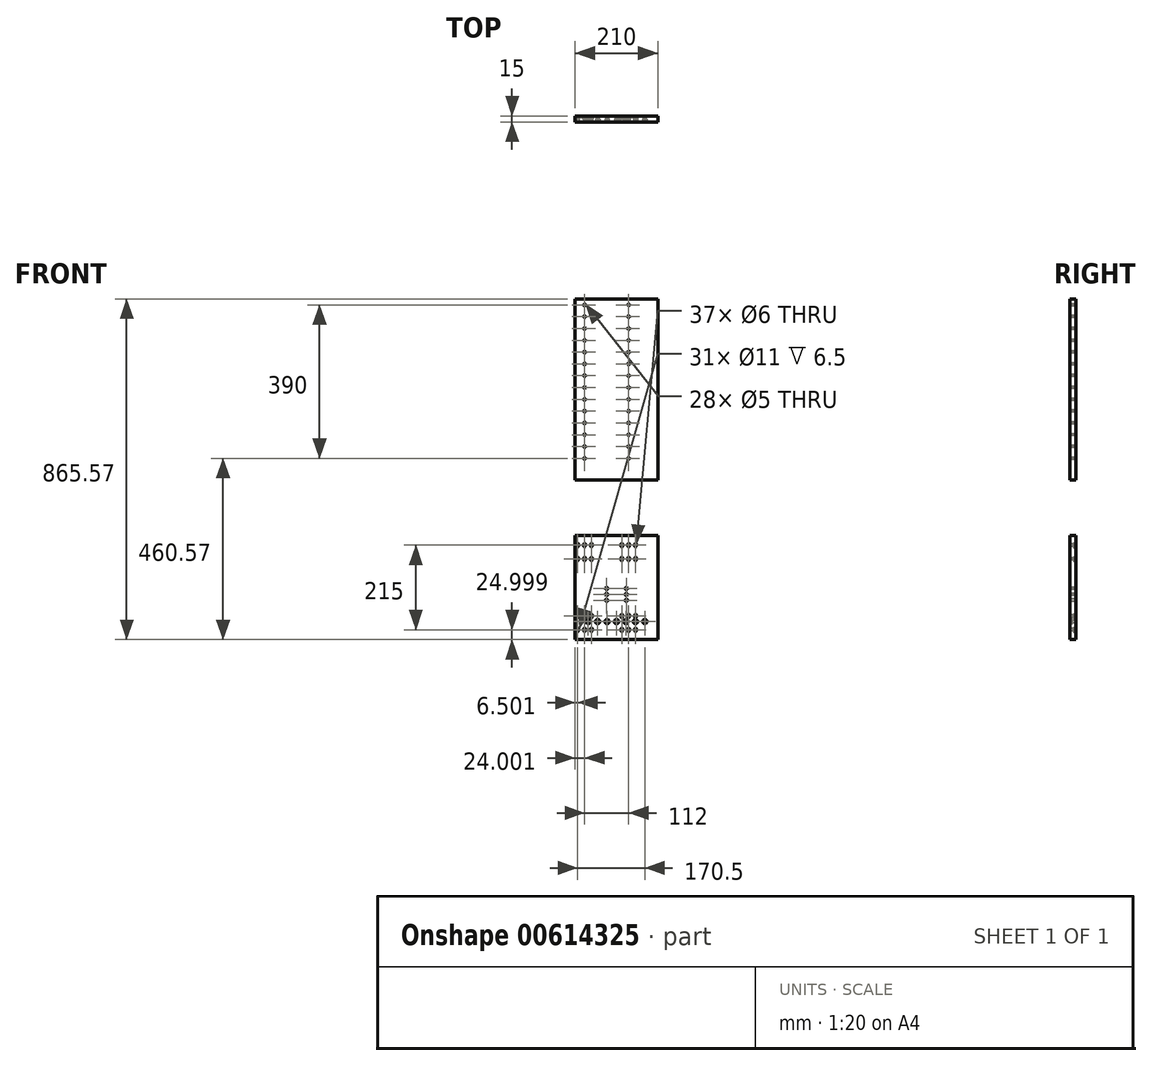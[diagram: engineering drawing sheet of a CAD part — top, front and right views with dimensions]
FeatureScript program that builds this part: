
annotation { "Feature Type Name" : "Feature", "Feature Type Description" : "" }
export const myFeature = defineFeature(function(context is Context, id is Id, definition is map)
    precondition{}
    {
        {
            var Q0;
            Q0=qCreatedBy(makeId("Front.planeOp"),FACE);
            var sketch = newSketch(context, id + "F0", { "sketchPlane" : qUnion([Q0])});
            skLineSegment(sketch, "E0.bottom", {"start": v(281.06, 612.26) * mm, "end": v(71.06, 612.26) * mm});
            skLineSegment(sketch, "E0.top", {"start": v(281.06, 152.26) * mm, "end": v(71.06, 152.26) * mm});
            skLineSegment(sketch, "E0.left", {"start": v(281.06, 612.26) * mm, "end": v(281.06, 152.26) * mm});
            skLineSegment(sketch, "E0.right", {"start": v(71.06, 612.26) * mm, "end": v(71.06, 152.26) * mm});
            skLineSegment(sketch, "E1.bottom", {"start": v(281.06, 11.69) * mm, "end": v(71.06, 11.69) * mm});
            skLineSegment(sketch, "E1.top", {"start": v(281.06, -253.31) * mm, "end": v(71.06, -253.31) * mm});
            skLineSegment(sketch, "E1.left", {"start": v(281.06, 11.69) * mm, "end": v(281.06, -253.31) * mm});
            skLineSegment(sketch, "E1.right", {"start": v(71.06, 11.69) * mm, "end": v(71.06, -253.31) * mm});
            skSolve(sketch);
        }
        {
            var Q0;
            Q0=makeQuery(id+"F0.imprint","IMPRINT",FACE,{"disambiguationData":[TD([[makeQuery(id+"F0.imprint","IMPRINT",EDGE,{"derivedFrom":sQuery(id+"F0.wireOp",EDGE,"E1.bottom")}),1.0]])]});
            var Q1;
            Q1=makeQuery(id+"F0.imprint","IMPRINT",FACE,{"disambiguationData":[TD([[makeQuery(id+"F0.imprint","IMPRINT",EDGE,{"derivedFrom":sQuery(id+"F0.wireOp",EDGE,"E0.bottom")}),1.0]])]});
            var Q2;
            Q2 = qSketchRegion(id + "F2HuvkIPk34AGJC_4", true);
            extrude(context, id + "F1", {"entities" : qUnion([Q0, Q1, Q2]), "depth" : 15 * mm, "offsetDistance" : 25 * mm});
        }
        {
            var Q0;
            Q0=makeQuery(id+"F1.opExtrude","CAP_FACE",FACE,{"disambiguationData":[OSD([sQuery(id+"F0.wireOp",EDGE,"E0.bottom"),sQuery(id+"F0.wireOp",EDGE,"E0.top"),sQuery(id+"F0.wireOp",EDGE,"E0.left"),sQuery(id+"F0.wireOp",EDGE,"E0.right")])],"isStart":false});
            var sketch = newSketch(context, id + "F2", { "sketchPlane" : qUnion([Q0])});
            skCircle(sketch, "E2", {"center": v(95.06, 597.26) * mm, "radius": 2.5 * mm});
            skCircle(sketch, "E3.0.1.0", {"center": v(95.06, 567.26) * mm, "radius": 2.5 * mm});
            skCircle(sketch, "E3.0.2.0", {"center": v(95.06, 537.26) * mm, "radius": 2.5 * mm});
            skCircle(sketch, "E3.0.3.0", {"center": v(95.06, 507.26) * mm, "radius": 2.5 * mm});
            skCircle(sketch, "E3.0.4.0", {"center": v(95.06, 477.26) * mm, "radius": 2.5 * mm});
            skCircle(sketch, "E3.0.5.0", {"center": v(95.06, 447.26) * mm, "radius": 2.5 * mm});
            skCircle(sketch, "E3.0.6.0", {"center": v(95.06, 417.26) * mm, "radius": 2.5 * mm});
            skCircle(sketch, "E3.0.7.0", {"center": v(95.06, 387.26) * mm, "radius": 2.5 * mm});
            skCircle(sketch, "E3.0.8.0", {"center": v(95.06, 357.26) * mm, "radius": 2.5 * mm});
            skCircle(sketch, "E3.0.9.0", {"center": v(95.06, 327.26) * mm, "radius": 2.5 * mm});
            skCircle(sketch, "E3.0.10.0", {"center": v(95.06, 297.26) * mm, "radius": 2.5 * mm});
            skCircle(sketch, "E3.0.11.0", {"center": v(95.06, 267.26) * mm, "radius": 2.5 * mm});
            skCircle(sketch, "E3.0.12.0", {"center": v(95.06, 237.26) * mm, "radius": 2.5 * mm});
            skCircle(sketch, "E3.0.13.0", {"center": v(95.06, 207.26) * mm, "radius": 2.5 * mm});
            skCircle(sketch, "E3.1.0.0", {"center": v(207.06, 597.26) * mm, "radius": 2.5 * mm});
            skCircle(sketch, "E3.1.1.0", {"center": v(207.06, 567.26) * mm, "radius": 2.5 * mm});
            skCircle(sketch, "E3.1.2.0", {"center": v(207.06, 537.26) * mm, "radius": 2.5 * mm});
            skCircle(sketch, "E3.1.3.0", {"center": v(207.06, 507.26) * mm, "radius": 2.5 * mm});
            skCircle(sketch, "E3.1.4.0", {"center": v(207.06, 477.26) * mm, "radius": 2.5 * mm});
            skCircle(sketch, "E3.1.5.0", {"center": v(207.06, 447.26) * mm, "radius": 2.5 * mm});
            skCircle(sketch, "E3.1.6.0", {"center": v(207.06, 417.26) * mm, "radius": 2.5 * mm});
            skCircle(sketch, "E3.1.7.0", {"center": v(207.06, 387.26) * mm, "radius": 2.5 * mm});
            skCircle(sketch, "E3.1.8.0", {"center": v(207.06, 357.26) * mm, "radius": 2.5 * mm});
            skCircle(sketch, "E3.1.9.0", {"center": v(207.06, 327.26) * mm, "radius": 2.5 * mm});
            skCircle(sketch, "E3.1.10.0", {"center": v(207.06, 297.26) * mm, "radius": 2.5 * mm});
            skCircle(sketch, "E3.1.11.0", {"center": v(207.06, 267.26) * mm, "radius": 2.5 * mm});
            skCircle(sketch, "E3.1.12.0", {"center": v(207.06, 237.26) * mm, "radius": 2.5 * mm});
            skCircle(sketch, "E3.1.13.0", {"center": v(207.06, 207.26) * mm, "radius": 2.5 * mm});
            skLineSegment(sketch, "E3.direction1", {"start": v(95.06, 597.26) * mm, "end": v(207.06, 597.26) * mm, "construction": true});
            skLineSegment(sketch, "E3.direction2", {"start": v(95.06, 597.26) * mm, "end": v(95.06, 567.26) * mm, "construction": true});
            skCircle(sketch, "E4", {"center": v(77.56, -228.31) * mm, "radius": 3 * mm});
            skCircle(sketch, "E5", {"center": v(151.06, -153.31) * mm, "radius": 3 * mm});
            skCircle(sketch, "E6.0.1.0", {"center": v(77.56, -193.31) * mm, "radius": 3 * mm});
            skCircle(sketch, "E6.1.0.0", {"center": v(95.06, -228.31) * mm, "radius": 3 * mm});
            skCircle(sketch, "E6.1.1.0", {"center": v(95.06, -193.31) * mm, "radius": 3 * mm});
            skCircle(sketch, "E6.2.0.0", {"center": v(112.56, -228.31) * mm, "radius": 3 * mm});
            skCircle(sketch, "E6.2.1.0", {"center": v(112.56, -193.31) * mm, "radius": 3 * mm});
            skLineSegment(sketch, "E6.direction1", {"start": v(77.56, -228.31) * mm, "end": v(95.06, -228.31) * mm, "construction": true});
            skLineSegment(sketch, "E6.direction2", {"start": v(77.56, -228.31) * mm, "end": v(77.56, -193.31) * mm, "construction": true});
            skCircle(sketch, "E7.0.1.0", {"center": v(151.06, -138.31) * mm, "radius": 3 * mm});
            skCircle(sketch, "E7.0.2.0", {"center": v(151.06, -123.31) * mm, "radius": 3 * mm});
            skCircle(sketch, "E7.1.0.0", {"center": v(201.06, -153.31) * mm, "radius": 3 * mm});
            skCircle(sketch, "E7.1.1.0", {"center": v(201.06, -138.31) * mm, "radius": 3 * mm});
            skCircle(sketch, "E7.1.2.0", {"center": v(201.06, -123.31) * mm, "radius": 3 * mm});
            skLineSegment(sketch, "E7.direction1", {"start": v(151.06, -153.31) * mm, "end": v(201.06, -153.31) * mm, "construction": true});
            skLineSegment(sketch, "E7.direction2", {"start": v(151.06, -153.31) * mm, "end": v(151.06, -138.31) * mm, "construction": true});
            skPoint(sketch, "E8", {"position": v(176.06, -153.31) * mm});
            skCircle(sketch, "E9.0.1.1", {"center": v(112.56, -48.31) * mm, "radius": 3 * mm});
            skCircle(sketch, "E9.0.1.3", {"center": v(112.56, -13.31) * mm, "radius": 3 * mm});
            skCircle(sketch, "E9.0.1.4", {"center": v(77.56, -13.31) * mm, "radius": 3 * mm});
            skCircle(sketch, "E9.0.1.6", {"center": v(95.06, -48.31) * mm, "radius": 3 * mm});
            skCircle(sketch, "E9.0.1.7", {"center": v(95.06, -13.31) * mm, "radius": 3 * mm});
            skCircle(sketch, "E9.0.1.9", {"center": v(77.56, -48.31) * mm, "radius": 3 * mm});
            skCircle(sketch, "E9.1.0.1", {"center": v(224.56, -228.31) * mm, "radius": 3 * mm});
            skCircle(sketch, "E9.1.0.3", {"center": v(224.56, -193.31) * mm, "radius": 3 * mm});
            skCircle(sketch, "E9.1.0.4", {"center": v(189.56, -193.31) * mm, "radius": 3 * mm});
            skCircle(sketch, "E9.1.0.6", {"center": v(207.06, -228.31) * mm, "radius": 3 * mm});
            skCircle(sketch, "E9.1.0.7", {"center": v(207.06, -193.31) * mm, "radius": 3 * mm});
            skCircle(sketch, "E9.1.0.9", {"center": v(189.56, -228.31) * mm, "radius": 3 * mm});
            skCircle(sketch, "E9.1.1.1", {"center": v(224.56, -48.31) * mm, "radius": 3 * mm});
            skCircle(sketch, "E9.1.1.3", {"center": v(224.56, -13.31) * mm, "radius": 3 * mm});
            skCircle(sketch, "E9.1.1.4", {"center": v(189.56, -13.31) * mm, "radius": 3 * mm});
            skCircle(sketch, "E9.1.1.6", {"center": v(207.06, -48.31) * mm, "radius": 3 * mm});
            skCircle(sketch, "E9.1.1.7", {"center": v(207.06, -13.31) * mm, "radius": 3 * mm});
            skCircle(sketch, "E9.1.1.9", {"center": v(189.56, -48.31) * mm, "radius": 3 * mm});
            skLineSegment(sketch, "E9.direction1", {"start": v(77.56, -228.31) * mm, "end": v(189.56, -228.31) * mm, "construction": true});
            skLineSegment(sketch, "E9.direction2", {"start": v(77.56, -228.31) * mm, "end": v(77.56, -48.31) * mm, "construction": true});
            skCircle(sketch, "E10", {"center": v(104.06, -207.31) * mm, "radius": 3 * mm});
            skCircle(sketch, "E11.1.0.0", {"center": v(128.06, -207.31) * mm, "radius": 3 * mm});
            skCircle(sketch, "E11.2.0.0", {"center": v(152.06, -207.31) * mm, "radius": 3 * mm});
            skCircle(sketch, "E11.3.0.0", {"center": v(176.06, -207.31) * mm, "radius": 3 * mm});
            skCircle(sketch, "E11.4.0.0", {"center": v(200.06, -207.31) * mm, "radius": 3 * mm});
            skCircle(sketch, "E11.5.0.0", {"center": v(224.06, -207.31) * mm, "radius": 3 * mm});
            skCircle(sketch, "E11.6.0.0", {"center": v(248.06, -207.31) * mm, "radius": 3 * mm});
            skLineSegment(sketch, "E11.direction1", {"start": v(104.06, -207.31) * mm, "end": v(128.06, -207.31) * mm, "construction": true});
            skSolve(sketch);
        }
        {
            var Q0;
            Q0 = qSketchRegion(id + "F2", true);
            extrude(context, id + "F3", {"entities" : qUnion([Q0]), "operationType" : NewBodyOperationType.REMOVE, "endBound" : BoundingType.UP_TO_NEXT, "oppositeDirection" : true, "depth" : 25 * mm, "offsetDistance" : 25 * mm});
        }
        {
            var Q0;
            Q0=makeQuery(id+"F1.opExtrude","CAP_FACE",FACE,{"disambiguationData":[OSD([sQuery(id+"F0.wireOp",EDGE,"E1.bottom"),sQuery(id+"F0.wireOp",EDGE,"E1.top"),sQuery(id+"F0.wireOp",EDGE,"E1.left"),sQuery(id+"F0.wireOp",EDGE,"E1.right")])],"isStart":false});
            var sketch = newSketch(context, id + "F4", { "sketchPlane" : qUnion([Q0])});
            skCircle(sketch, "E12", {"center": v(104.06, -207.31) * mm, "radius": 5.5 * mm});
            skCircle(sketch, "E13", {"center": v(128.06, -207.31) * mm, "radius": 5.5 * mm});
            skCircle(sketch, "E14", {"center": v(152.06, -207.31) * mm, "radius": 5.5 * mm});
            skCircle(sketch, "E15", {"center": v(176.06, -207.31) * mm, "radius": 5.5 * mm});
            skCircle(sketch, "E16", {"center": v(200.06, -207.31) * mm, "radius": 5.5 * mm});
            skCircle(sketch, "E17", {"center": v(224.06, -207.31) * mm, "radius": 5.5 * mm});
            skCircle(sketch, "E18", {"center": v(248.06, -207.31) * mm, "radius": 5.5 * mm});
            skSolve(sketch);
        }
        {
            var Q0;
            Q0=makeQuery(id+"F4.imprint","IMPRINT",FACE,{"disambiguationData":[TD([[makeQuery(id+"F4.imprint","IMPRINT",EDGE,{"derivedFrom":sQuery(id+"F4.wireOp",EDGE,"E12")}),1.0]])]});
            var Q1;
            Q1=makeQuery(id+"F4.imprint","IMPRINT",FACE,{"disambiguationData":[TD([[makeQuery(id+"F4.imprint","IMPRINT",EDGE,{"derivedFrom":sQuery(id+"F4.wireOp",EDGE,"E13")}),1.0]])]});
            var Q2;
            Q2=makeQuery(id+"F4.imprint","IMPRINT",FACE,{"disambiguationData":[TD([[makeQuery(id+"F4.imprint","IMPRINT",EDGE,{"derivedFrom":sQuery(id+"F4.wireOp",EDGE,"E14")}),1.0]])]});
            var Q3;
            Q3=makeQuery(id+"F4.imprint","IMPRINT",FACE,{"disambiguationData":[TD([[makeQuery(id+"F4.imprint","IMPRINT",EDGE,{"derivedFrom":sQuery(id+"F4.wireOp",EDGE,"E15")}),1.0]])]});
            var Q4;
            Q4=makeQuery(id+"F4.imprint","IMPRINT",FACE,{"disambiguationData":[TD([[makeQuery(id+"F4.imprint","IMPRINT",EDGE,{"derivedFrom":sQuery(id+"F4.wireOp",EDGE,"E18")}),1.0]])]});
            var Q5;
            Q5=makeQuery(id+"F4.imprint","IMPRINT",FACE,{"disambiguationData":[TD([[makeQuery(id+"F4.imprint","IMPRINT",EDGE,{"derivedFrom":sQuery(id+"F4.wireOp",EDGE,"E16")}),1.0]])]});
            var Q6;
            Q6=makeQuery(id+"F4.imprint","IMPRINT",FACE,{"disambiguationData":[TD([[makeQuery(id+"F4.imprint","IMPRINT",EDGE,{"derivedFrom":sQuery(id+"F4.wireOp",EDGE,"E17")}),1.0]])]});
            extrude(context, id + "F5", {"entities" : qUnion([Q0, Q1, Q2, Q3, Q4, Q5, Q6]), "operationType" : NewBodyOperationType.REMOVE, "oppositeDirection" : true, "depth" : 6.5 * mm, "offsetDistance" : 25 * mm});
        }
        {
            var Q0;
            Q0=makeQuery(id+"F1.opExtrude","CAP_FACE",FACE,{"disambiguationData":[OSD([sQuery(id+"F0.wireOp",EDGE,"E1.bottom"),sQuery(id+"F0.wireOp",EDGE,"E1.top"),sQuery(id+"F0.wireOp",EDGE,"E1.left"),sQuery(id+"F0.wireOp",EDGE,"E1.right")])],"isStart":true});
            var sketch = newSketch(context, id + "F6", { "sketchPlane" : qUnion([Q0])});
            skCircle(sketch, "E19", {"center": v(-224.56, -228.31) * mm, "radius": 5.5 * mm});
            skCircle(sketch, "E20", {"center": v(-207.06, -228.31) * mm, "radius": 5.5 * mm});
            skCircle(sketch, "E21", {"center": v(-189.56, -228.31) * mm, "radius": 5.5 * mm});
            skCircle(sketch, "E22", {"center": v(-112.56, -228.31) * mm, "radius": 5.5 * mm});
            skCircle(sketch, "E23", {"center": v(-95.06, -228.31) * mm, "radius": 5.5 * mm});
            skCircle(sketch, "E24", {"center": v(-77.56, -228.31) * mm, "radius": 5.5 * mm});
            skCircle(sketch, "E25", {"center": v(-224.56, -48.31) * mm, "radius": 5.5 * mm});
            skCircle(sketch, "E26", {"center": v(-207.06, -48.31) * mm, "radius": 5.5 * mm});
            skCircle(sketch, "E27", {"center": v(-189.56, -48.31) * mm, "radius": 5.5 * mm});
            skCircle(sketch, "E28", {"center": v(-224.56, -13.31) * mm, "radius": 5.5 * mm});
            skCircle(sketch, "E29", {"center": v(-207.06, -13.31) * mm, "radius": 5.5 * mm});
            skCircle(sketch, "E30", {"center": v(-189.56, -13.31) * mm, "radius": 5.5 * mm});
            skCircle(sketch, "E31", {"center": v(-224.56, -193.31) * mm, "radius": 5.5 * mm});
            skCircle(sketch, "E32", {"center": v(-207.06, -193.31) * mm, "radius": 5.5 * mm});
            skCircle(sketch, "E33", {"center": v(-189.56, -193.31) * mm, "radius": 5.5 * mm});
            skCircle(sketch, "E34", {"center": v(-112.56, -193.31) * mm, "radius": 5.5 * mm});
            skCircle(sketch, "E35", {"center": v(-95.06, -193.31) * mm, "radius": 5.5 * mm});
            skCircle(sketch, "E36", {"center": v(-77.56, -193.31) * mm, "radius": 5.5 * mm});
            skCircle(sketch, "E37", {"center": v(-112.56, -13.31) * mm, "radius": 5.5 * mm});
            skCircle(sketch, "E38", {"center": v(-95.06, -13.31) * mm, "radius": 5.5 * mm});
            skCircle(sketch, "E39", {"center": v(-77.56, -13.31) * mm, "radius": 5.5 * mm});
            skCircle(sketch, "E40", {"center": v(-112.56, -48.31) * mm, "radius": 5.5 * mm});
            skCircle(sketch, "E41", {"center": v(-95.06, -48.31) * mm, "radius": 5.5 * mm});
            skCircle(sketch, "E42", {"center": v(-77.56, -48.31) * mm, "radius": 5.5 * mm});
            skSolve(sketch);
        }
        {
            var Q0;
            Q0=makeQuery(id+"F6.imprint","IMPRINT",FACE,{"disambiguationData":[TD([[makeQuery(id+"F6.imprint","IMPRINT",EDGE,{"derivedFrom":sQuery(id+"F6.wireOp",EDGE,"E19")}),1.0]])]});
            var Q1;
            Q1=makeQuery(id+"F6.imprint","IMPRINT",FACE,{"disambiguationData":[TD([[makeQuery(id+"F6.imprint","IMPRINT",EDGE,{"derivedFrom":sQuery(id+"F6.wireOp",EDGE,"E20")}),1.0]])]});
            var Q2;
            Q2=makeQuery(id+"F6.imprint","IMPRINT",FACE,{"disambiguationData":[TD([[makeQuery(id+"F6.imprint","IMPRINT",EDGE,{"derivedFrom":sQuery(id+"F6.wireOp",EDGE,"E21")}),1.0]])]});
            var Q3;
            Q3=makeQuery(id+"F6.imprint","IMPRINT",FACE,{"disambiguationData":[TD([[makeQuery(id+"F6.imprint","IMPRINT",EDGE,{"derivedFrom":sQuery(id+"F6.wireOp",EDGE,"E28")}),1.0]])]});
            var Q4;
            Q4=makeQuery(id+"F6.imprint","IMPRINT",FACE,{"disambiguationData":[TD([[makeQuery(id+"F6.imprint","IMPRINT",EDGE,{"derivedFrom":sQuery(id+"F6.wireOp",EDGE,"E29")}),1.0]])]});
            var Q5;
            Q5=makeQuery(id+"F6.imprint","IMPRINT",FACE,{"disambiguationData":[TD([[makeQuery(id+"F6.imprint","IMPRINT",EDGE,{"derivedFrom":sQuery(id+"F6.wireOp",EDGE,"E30")}),1.0]])]});
            var Q6;
            Q6=makeQuery(id+"F6.imprint","IMPRINT",FACE,{"disambiguationData":[TD([[makeQuery(id+"F6.imprint","IMPRINT",EDGE,{"derivedFrom":sQuery(id+"F6.wireOp",EDGE,"E27")}),1.0]])]});
            var Q7;
            Q7=makeQuery(id+"F6.imprint","IMPRINT",FACE,{"disambiguationData":[TD([[makeQuery(id+"F6.imprint","IMPRINT",EDGE,{"derivedFrom":sQuery(id+"F6.wireOp",EDGE,"E26")}),1.0]])]});
            var Q8;
            Q8=makeQuery(id+"F6.imprint","IMPRINT",FACE,{"disambiguationData":[TD([[makeQuery(id+"F6.imprint","IMPRINT",EDGE,{"derivedFrom":sQuery(id+"F6.wireOp",EDGE,"E25")}),1.0]])]});
            var Q9;
            Q9=makeQuery(id+"F6.imprint","IMPRINT",FACE,{"disambiguationData":[TD([[makeQuery(id+"F6.imprint","IMPRINT",EDGE,{"derivedFrom":sQuery(id+"F6.wireOp",EDGE,"E22")}),1.0]])]});
            var Q10;
            Q10=makeQuery(id+"F6.imprint","IMPRINT",FACE,{"disambiguationData":[TD([[makeQuery(id+"F6.imprint","IMPRINT",EDGE,{"derivedFrom":sQuery(id+"F6.wireOp",EDGE,"E23")}),1.0]])]});
            var Q11;
            Q11=makeQuery(id+"F6.imprint","IMPRINT",FACE,{"disambiguationData":[TD([[makeQuery(id+"F6.imprint","IMPRINT",EDGE,{"derivedFrom":sQuery(id+"F6.wireOp",EDGE,"E24")}),1.0]])]});
            var Q12;
            Q12=makeQuery(id+"F6.imprint","IMPRINT",FACE,{"disambiguationData":[TD([[makeQuery(id+"F6.imprint","IMPRINT",EDGE,{"derivedFrom":sQuery(id+"F6.wireOp",EDGE,"E34")}),1.0]])]});
            var Q13;
            Q13=makeQuery(id+"F6.imprint","IMPRINT",FACE,{"disambiguationData":[TD([[makeQuery(id+"F6.imprint","IMPRINT",EDGE,{"derivedFrom":sQuery(id+"F6.wireOp",EDGE,"E35")}),1.0]])]});
            var Q14;
            Q14=makeQuery(id+"F6.imprint","IMPRINT",FACE,{"disambiguationData":[TD([[makeQuery(id+"F6.imprint","IMPRINT",EDGE,{"derivedFrom":sQuery(id+"F6.wireOp",EDGE,"E36")}),1.0]])]});
            var Q15;
            Q15=makeQuery(id+"F6.imprint","IMPRINT",FACE,{"disambiguationData":[TD([[makeQuery(id+"F6.imprint","IMPRINT",EDGE,{"derivedFrom":sQuery(id+"F6.wireOp",EDGE,"E33")}),1.0]])]});
            var Q16;
            Q16=makeQuery(id+"F6.imprint","IMPRINT",FACE,{"disambiguationData":[TD([[makeQuery(id+"F6.imprint","IMPRINT",EDGE,{"derivedFrom":sQuery(id+"F6.wireOp",EDGE,"E32")}),1.0]])]});
            var Q17;
            Q17=makeQuery(id+"F6.imprint","IMPRINT",FACE,{"disambiguationData":[TD([[makeQuery(id+"F6.imprint","IMPRINT",EDGE,{"derivedFrom":sQuery(id+"F6.wireOp",EDGE,"E31")}),1.0]])]});
            var Q18;
            Q18=makeQuery(id+"F6.imprint","IMPRINT",FACE,{"disambiguationData":[TD([[makeQuery(id+"F6.imprint","IMPRINT",EDGE,{"derivedFrom":sQuery(id+"F6.wireOp",EDGE,"E40")}),1.0]])]});
            var Q19;
            Q19=makeQuery(id+"F6.imprint","IMPRINT",FACE,{"disambiguationData":[TD([[makeQuery(id+"F6.imprint","IMPRINT",EDGE,{"derivedFrom":sQuery(id+"F6.wireOp",EDGE,"E41")}),1.0]])]});
            var Q20;
            Q20=makeQuery(id+"F6.imprint","IMPRINT",FACE,{"disambiguationData":[TD([[makeQuery(id+"F6.imprint","IMPRINT",EDGE,{"derivedFrom":sQuery(id+"F6.wireOp",EDGE,"E42")}),1.0]])]});
            var Q21;
            Q21=makeQuery(id+"F6.imprint","IMPRINT",FACE,{"disambiguationData":[TD([[makeQuery(id+"F6.imprint","IMPRINT",EDGE,{"derivedFrom":sQuery(id+"F6.wireOp",EDGE,"E39")}),1.0]])]});
            var Q22;
            Q22=makeQuery(id+"F6.imprint","IMPRINT",FACE,{"disambiguationData":[TD([[makeQuery(id+"F6.imprint","IMPRINT",EDGE,{"derivedFrom":sQuery(id+"F6.wireOp",EDGE,"E38")}),1.0]])]});
            var Q23;
            Q23=makeQuery(id+"F6.imprint","IMPRINT",FACE,{"disambiguationData":[TD([[makeQuery(id+"F6.imprint","IMPRINT",EDGE,{"derivedFrom":sQuery(id+"F6.wireOp",EDGE,"E37")}),1.0]])]});
            extrude(context, id + "F7", {"entities" : qUnion([Q0, Q1, Q2, Q3, Q4, Q5, Q6, Q7, Q8, Q9, Q10, Q11, Q12, Q13, Q14, Q15, Q16, Q17, Q18, Q19, Q20, Q21, Q22, Q23]), "operationType" : NewBodyOperationType.REMOVE, "oppositeDirection" : true, "depth" : 6.5 * mm, "offsetDistance" : 25 * mm});
        }
    });
